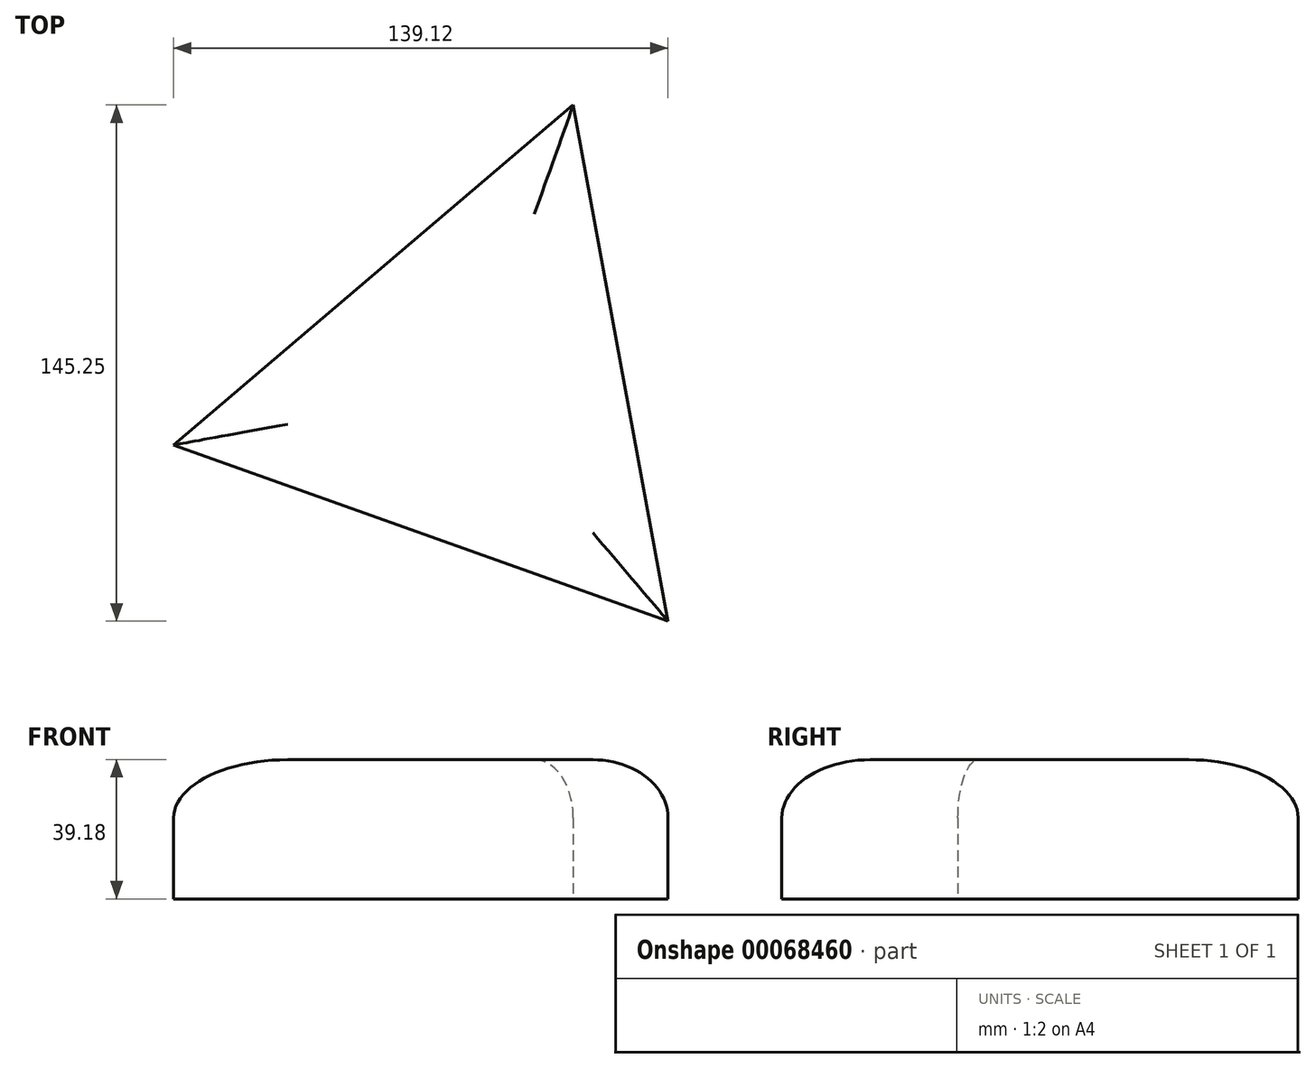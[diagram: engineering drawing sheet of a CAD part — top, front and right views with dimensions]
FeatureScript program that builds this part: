
annotation { "Feature Type Name" : "Feature", "Feature Type Description" : "" }
export const myFeature = defineFeature(function(context is Context, id is Id, definition is map)
    precondition{}
    {
        {
            var Q0;
            Q0=qCreatedBy(makeId("Top.planeOp"),FACE);
            var sketch = newSketch(context, id + "F0", { "sketchPlane" : qUnion([Q0])});
            skCircle(sketch, "E0.cCircle", {"center": v(0, 0) * mm, "radius": 42.63 * mm, "construction": true});
            skLineSegment(sketch, "E0.0", {"start": v(28.6, 80.32) * mm, "end": v(55.26, -64.93) * mm});
            skLineSegment(sketch, "E0.1", {"start": v(55.26, -64.93) * mm, "end": v(-83.86, -15.4) * mm});
            skLineSegment(sketch, "E0.2", {"start": v(-83.86, -15.4) * mm, "end": v(28.6, 80.32) * mm});
            skPoint(sketch, "E0.0.midPoint", {"position": v(41.93, 7.7) * mm});
            skSolve(sketch);
        }
        {
            var Q0;
            Q0=makeQuery(id+"F0.imprint","IMPRINT",FACE,{"disambiguationData":[TD([[makeQuery(id+"F0.imprint","IMPRINT",EDGE,{"derivedFrom":sQuery(id+"F0.wireOp",EDGE,"E0.0")}),-1.0]])]});
            extrude(context, id + "F1", {"entities" : qUnion([Q0]), "depth" : 39.18 * mm});
        }
        {
            var Q0;
            Q0=makeQuery(id+"F1.opExtrude","CAP_EDGE",EDGE,{"disambiguationData":[OSD([sQuery(id+"F0.wireOp",EDGE,"E0.0")])],"isStart":false});
            var Q1;
            Q1=makeQuery(id+"F1.opExtrude","CAP_EDGE",EDGE,{"disambiguationData":[OSD([sQuery(id+"F0.wireOp",EDGE,"E0.1")])],"isStart":false});
            var Q2;
            Q2=makeQuery(id+"F1.opExtrude","CAP_FACE",FACE,{"disambiguationData":[OSD([sQuery(id+"F0.wireOp",EDGE,"E0.0"),sQuery(id+"F0.wireOp",EDGE,"E0.1"),sQuery(id+"F0.wireOp",EDGE,"E0.2")])],"isStart":false});
            fillet(context, id + "F2", {"entities" : qUnion([Q0, Q1, Q2]), "radius" : 16.32 * mm, "tangentPropagation" : true, "allowEdgeOverflow" : false});
        }
        {
            var Q0;
            Q0=makeQuery(id+"F1.opExtrude","CAP_FACE",FACE,{"disambiguationData":[OSD([sQuery(id+"F0.wireOp",EDGE,"E0.0"),sQuery(id+"F0.wireOp",EDGE,"E0.1"),sQuery(id+"F0.wireOp",EDGE,"E0.2")])],"isStart":true});
            var sketch = newSketch(context, id + "F3", { "sketchPlane" : qUnion([Q0])});
            skCircle(sketch, "E1", {"center": v(0, 0) * mm, "radius": 30.1 * mm});
            skSolve(sketch);
        }
        {
            var Q0;
            Q0=makeQuery(id+"F3.imprint","IMPRINT",FACE,{"disambiguationData":[TD([[makeQuery(id+"F3.imprint","IMPRINT",EDGE,{"derivedFrom":sQuery(id+"F3.wireOp",EDGE,"E1")}),1.0]])]});
            extrude(context, id + "F4", {"entities" : qUnion([Q0]), "operationType" : NewBodyOperationType.ADD, "oppositeDirection" : true, "depth" : 30.1 * mm});
        }
        {
            var Q0;
            Q0=qCreatedBy(makeId("Top.planeOp"),FACE);
            var sketch = newSketch(context, id + "F5", { "sketchPlane" : qUnion([Q0])});
            skCircle(sketch, "E2.cCircle", {"center": v(0, 0) * mm, "radius": 32.53 * mm, "construction": true});
            skLineSegment(sketch, "E2.0", {"start": v(32.1, -12.98) * mm, "end": v(16.24, -30.58) * mm});
            skLineSegment(sketch, "E2.1", {"start": v(16.24, -30.58) * mm, "end": v(-7.21, -33.86) * mm});
            skLineSegment(sketch, "E2.2", {"start": v(-7.21, -33.86) * mm, "end": v(-27.3, -21.3) * mm});
            skLineSegment(sketch, "E2.3", {"start": v(-27.3, -21.3) * mm, "end": v(-34.6, 1.22) * mm});
            skLineSegment(sketch, "E2.4", {"start": v(-34.6, 1.22) * mm, "end": v(-25.72, 23.18) * mm});
            skLineSegment(sketch, "E2.5", {"start": v(-25.72, 23.18) * mm, "end": v(-4.8, 34.29) * mm});
            skLineSegment(sketch, "E2.6", {"start": v(-4.8, 34.29) * mm, "end": v(18.36, 29.35) * mm});
            skLineSegment(sketch, "E2.7", {"start": v(18.36, 29.35) * mm, "end": v(32.93, 10.68) * mm});
            skLineSegment(sketch, "E2.8", {"start": v(32.93, 10.68) * mm, "end": v(32.1, -12.98) * mm});
            skPoint(sketch, "E2.0.midPoint", {"position": v(24.17, -21.78) * mm});
            skSolve(sketch);
        }
        {
            var Q0;
            Q0=makeQuery(id+"F5.imprint","IMPRINT",FACE,{"disambiguationData":[TD([[makeQuery(id+"F5.imprint","IMPRINT",EDGE,{"derivedFrom":sQuery(id+"F5.wireOp",EDGE,"E2.0")}),-1.0]])]});
            extrude(context, id + "F6", {"entities" : qUnion([Q0]), "operationType" : NewBodyOperationType.ADD, "depth" : 27 * mm});
        }
    });
